FCSTD DOCUMENT  (FreeCAD 0.19R24291 (Git))
Label: Problem 10
License: All rights reserved
LicenseURL: http://en.wikipedia.org/wiki/All_rights_reserved
objects: Part::Part2DObjectPython×50, App::FeaturePython×45
note: 50 computed .brp shape members not serialized (recipe doc carries the construction recipe); baked Part::Feature solids carry a one-line shape summary decoded from their .brp

FEATURE [Part::Part2DObjectPython] Line  # Draft 2D object (typed FeaturePython)
  Area = 0
  ChamferSize = 0
  Closed = false
  End = (-61.5574,-5.46448,0)
  FilletRadius = 0
  Length = 23.4862
  MakeFace = false
  Placement = pos=(-143.431,-5.46448,0) rot=(0,0,1;0rad)
  Points = (2) [(58.3871,-3.55271e-15,0),(81.8734,-4.44089e-15,0)]
  Start = (-85.0436,-5.46448,0)
  Subdivisions = 0
FEATURE [Part::Part2DObjectPython] Wire  # Draft 2D object (typed FeaturePython)
  Area = 0
  ChamferSize = 0
  Closed = false
  End = (122.991,-5.46448,0)
  FilletRadius = 0
  Length = 125.6
  MakeFace = false
  Placement = pos=(-2.6087,-5.46448,0) rot=(0,0,1;0rad)
  Points = (3) [(0,0,0),(0,0,0),(125.6,3.55271e-15,0)]
  Start = (-2.6087,-5.46448,0)
  Subdivisions = 7
FEATURE [Part::Part2DObjectPython] Line008  # Draft 2D object (typed FeaturePython)
  Area = 0
  ChamferSize = 0
  Closed = false
  End = (-2.6087,13.1231,0)
  FilletRadius = 0
  Length = 18.5876
  MakeFace = false
  Placement = pos=(-2.6087,-5.46448,0) rot=(0,0,1;0rad)
  Points = (2) [(0,0,0),(4.44089e-16,18.5876,0)]
  Start = (-2.6087,-5.46448,0)
  Subdivisions = 0
FEATURE [Part::Part2DObjectPython] Line009  # Draft 2D object (typed FeaturePython)
  Area = 0
  ChamferSize = 0
  Closed = false
  End = (122.991,44.5355,0)
  FilletRadius = 0
  Length = 125.6
  MakeFace = false
  Points = (2) [(-2.6087,44.5355,0),(122.991,44.5355,0)]
  Start = (-2.6087,44.5355,0)
  Subdivisions = 0
FEATURE [Part::Part2DObjectPython] Line010  # Draft 2D object (typed FeaturePython)
  Area = 0
  ChamferSize = 0
  Closed = false
  End = (122.991,13.1231,0)
  FilletRadius = 0
  Length = 18.5876
  MakeFace = false
  Points = (2) [(122.991,-5.46448,0),(122.991,13.1231,0)]
  Start = (122.991,-5.46448,0)
  Subdivisions = 0
FEATURE [Part::Part2DObjectPython] Line011  # Draft 2D object (typed FeaturePython)
  Area = 0
  ChamferSize = 0
  Closed = false
  End = (60.1913,44.5355,0)
  FilletRadius = 0
  Length = 50
  MakeFace = false
  Placement = pos=(60.1913,-5.46448,0) rot=(0,0,1;0rad)
  Points = (2) [(0,0,0),(0,50,0)]
  Start = (60.1913,-5.46448,0)
  Subdivisions = 0
FEATURE [Part::Part2DObjectPython] Line012  # Draft 2D object (typed FeaturePython)
  Area = 0
  ChamferSize = 0
  Closed = false
  End = (13.0913,44.5355,0)
  FilletRadius = 0
  Length = 50
  MakeFace = false
  Placement = pos=(13.0913,-5.46448,0) rot=(0,0,1;0rad)
  Points = (2) [(0,0,0),(1.77636e-15,50,0)]
  Start = (13.0913,-5.46448,0)
  Subdivisions = 0
FEATURE [Part::Part2DObjectPython] Line013  # Draft 2D object (typed FeaturePython)
  Area = 0
  ChamferSize = 0
  Closed = false
  End = (28.7913,44.5355,0)
  FilletRadius = 0
  Length = 50
  MakeFace = false
  Placement = pos=(28.7913,-5.46448,0) rot=(0,0,1;0rad)
  Points = (2) [(0,0,0),(3.55271e-15,50,0)]
  Start = (28.7913,-5.46448,0)
  Subdivisions = 0
FEATURE [Part::Part2DObjectPython] Line014  # Draft 2D object (typed FeaturePython)
  Area = 0
  ChamferSize = 0
  Closed = false
  End = (44.4913,44.5355,0)
  FilletRadius = 0
  Length = 50
  MakeFace = false
  Placement = pos=(44.4913,-5.46448,0) rot=(0,0,1;0rad)
  Points = (2) [(0,0,0),(0,50,0)]
  Start = (44.4913,-5.46448,0)
  Subdivisions = 0
FEATURE [Part::Part2DObjectPython] Line015  # Draft 2D object (typed FeaturePython)
  Area = 0
  ChamferSize = 0
  Closed = false
  End = (75.8913,44.5355,0)
  FilletRadius = 0
  Length = 50
  MakeFace = false
  Placement = pos=(75.8913,-5.46448,0) rot=(0,0,1;0rad)
  Points = (2) [(0,0,0),(1.42109e-14,50,0)]
  Start = (75.8913,-5.46448,0)
  Subdivisions = 0
FEATURE [Part::Part2DObjectPython] Line016  # Draft 2D object (typed FeaturePython)
  Area = 0
  ChamferSize = 0
  Closed = false
  End = (91.5913,44.5355,0)
  FilletRadius = 0
  Length = 50
  MakeFace = false
  Placement = pos=(91.5913,-5.46448,0) rot=(0,0,1;0rad)
  Points = (2) [(0,0,0),(0,50,0)]
  Start = (91.5913,-5.46448,0)
  Subdivisions = 0
FEATURE [Part::Part2DObjectPython] Line017  # Draft 2D object (typed FeaturePython)
  Area = 0
  ChamferSize = 0
  Closed = false
  End = (107.291,44.5355,0)
  FilletRadius = 0
  Length = 50
  MakeFace = false
  Placement = pos=(107.291,-5.46448,0) rot=(0,0,1;0rad)
  Points = (2) [(0,0,0),(0,50,0)]
  Start = (107.291,-5.46448,0)
  Subdivisions = 0
FEATURE [Part::Part2DObjectPython] Circle  # Draft 2D object (typed FeaturePython)
  Area = 0
  FirstAngle = 0
  LastAngle = 0
  MakeFace = false
  Placement = pos=(-41.5574,-31.4208,0) rot=(0,0,1;0rad)
  Radius = 20
FEATURE [Part::Part2DObjectPython] Line018  # Draft 2D object (typed FeaturePython)
  Area = 0
  ChamferSize = 0
  Closed = false
  End = (-61.5574,-31.4208,0)
  FilletRadius = 0
  Length = 0
  MakeFace = false
  Placement = pos=(-61.5574,-31.4208,0) rot=(0,0,1;0rad)
  Points = (2) [(0,0,0),(0,-3.55271e-15,0)]
  Start = (-61.5574,-31.4208,0)
  Subdivisions = 0
FEATURE [Part::Part2DObjectPython] Line019  # Draft 2D object (typed FeaturePython)
  Area = 0
  ChamferSize = 0
  Closed = false
  End = (-61.6814,13.0515,0)
  FilletRadius = 0
  Length = 18.5161
  MakeFace = false
  Placement = pos=(-61.5574,-31.4208,0) rot=(0,0,1;0rad)
  Points = (2) [(-0.196875,25.9563,0),(-0.123968,44.4723,0)]
  Start = (-61.7543,-5.46448,0)
  Subdivisions = 0
FEATURE [Part::Part2DObjectPython] Line020  # Draft 2D object (typed FeaturePython)
  Area = 0
  ChamferSize = 0
  Closed = false
  End = (-41.5574,-5.46448,0)
  FilletRadius = 0
  Length = 50
  MakeFace = false
  Placement = pos=(-41.5574,-51.4208,0) rot=(0,0,1;0rad)
  Points = (2) [(-7.10543e-15,95.9563,0),(0,45.9563,0)]
  Start = (-41.5574,44.5355,0)
  Subdivisions = 0
FEATURE [Part::Part2DObjectPython] Line021  # Draft 2D object (typed FeaturePython)
  Area = 0
  ChamferSize = 0
  Closed = false
  End = (-55.6995,-5.46448,0)
  FilletRadius = 0
  Length = 50
  MakeFace = false
  Placement = pos=(-55.6995,-45.5629,0) rot=(0,0,1;0rad)
  Points = (2) [(0,90.0984,0),(0,40.0984,0)]
  Start = (-55.6995,44.5355,0)
  Subdivisions = 0
FEATURE [Part::Part2DObjectPython] Line022  # Draft 2D object (typed FeaturePython)
  Area = 0
  ChamferSize = 0
  Closed = false
  End = (-27.4152,-5.46448,0)
  FilletRadius = 0
  Length = 50
  MakeFace = false
  Placement = pos=(-27.4152,-45.5629,0) rot=(0,0,1;0rad)
  Points = (2) [(-1.42109e-14,90.0984,0),(0,40.0984,0)]
  Start = (-27.4152,44.5355,0)
  Subdivisions = 0
FEATURE [Part::Part2DObjectPython] Line023  # Draft 2D object (typed FeaturePython)
  Area = 0
  ChamferSize = 0
  Closed = false
  End = (-21.5574,36.2171,0)
  FilletRadius = 0
  Length = 8.31841
  MakeFace = false
  Placement = pos=(-21.5574,-31.4208,0) rot=(0,0,1;0rad)
  Points = (2) [(-4.26326e-14,75.9563,0),(-2.4869e-14,67.6379,0)]
  Start = (-21.5574,44.5355,0)
  Subdivisions = 0
FEATURE [Part::Part2DObjectPython] Line024  # Draft 2D object (typed FeaturePython)
  Area = 0
  ChamferSize = 0
  Closed = false
  End = (-61.5574,44.5355,0)
  FilletRadius = 0
  Length = 40
  MakeFace = false
  Placement = pos=(-21.5574,44.5355,0) rot=(0,0,1;0rad)
  Points = (2) [(0,0,0),(-40,-7.10543e-15,0)]
  Start = (-21.5574,44.5355,0)
  Subdivisions = 0
FEATURE [Part::Part2DObjectPython] Line026  # Draft 2D object (typed FeaturePython)
  Area = 0
  ChamferSize = 0
  Closed = false
  End = (-21.5574,36.2171,0)
  FilletRadius = 0
  Length = 11.8769
  MakeFace = false
  Placement = pos=(-41.5886,24.6521,0) rot=(0,0,1;0.523599rad)
  Points = (2) [(35.007,2.13163e-14,0),(23.1301,2.84217e-14,0)]
  Start = (-11.2717,42.1556,0)
  Subdivisions = 0
FEATURE [Part::Part2DObjectPython] Line027  # Draft 2D object (typed FeaturePython)
  Area = 0
  ChamferSize = 0
  Closed = false
  End = (122.991,13.1231,0)
  FilletRadius = 0
  Length = 184.549
  MakeFace = false
  Placement = pos=(-61.5574,13.1231,0) rot=(0,0,1;0rad)
  Points = (2) [(0,0,0),(184.549,-5.32907e-15,0)]
  Start = (-61.5574,13.1231,0)
  Subdivisions = 0
FEATURE [Part::Part2DObjectPython] Line028  # Draft 2D object (typed FeaturePython)
  Area = 0
  ChamferSize = 0
  Closed = false
  End = (122.991,16.5051,0)
  FilletRadius = 0
  Length = 178.691
  MakeFace = false
  Placement = pos=(-55.6995,16.5051,0) rot=(0,0,1;0rad)
  Points = (2) [(0,0,0),(178.691,1.06581e-14,0)]
  Start = (-55.6995,16.5051,0)
  Subdivisions = 0
FEATURE [Part::Part2DObjectPython] Line029  # Draft 2D object (typed FeaturePython)
  Area = 0
  ChamferSize = 0
  Closed = false
  End = (122.991,24.6701,0)
  FilletRadius = 0
  Length = 164.549
  MakeFace = false
  Placement = pos=(-41.5574,24.6701,0) rot=(0,0,1;0rad)
  Points = (2) [(0,0,0),(164.549,-7.10543e-15,0)]
  Start = (-41.5574,24.6701,0)
  Subdivisions = 0
FEATURE [Part::Part2DObjectPython] Line030  # Draft 2D object (typed FeaturePython)
  Area = 0
  ChamferSize = 0
  Closed = false
  End = (122.991,32.8351,0)
  FilletRadius = 0
  Length = 150.407
  MakeFace = false
  Placement = pos=(-27.4152,32.8351,0) rot=(0,0,1;0rad)
  Points = (2) [(0,0,0),(150.407,-7.10543e-15,0)]
  Start = (-27.4152,32.8351,0)
  Subdivisions = 0
FEATURE [Part::Part2DObjectPython] Line031  # Draft 2D object (typed FeaturePython)
  Area = 0
  ChamferSize = 0
  Closed = false
  End = (122.991,36.2171,0)
  FilletRadius = 0
  Length = 144.549
  MakeFace = false
  Placement = pos=(-21.5574,36.2171,0) rot=(0,0,1;0rad)
  Points = (2) [(0,0,0),(144.549,7.10543e-15,0)]
  Start = (-21.5574,36.2171,0)
  Subdivisions = 0
FEATURE [Part::Part2DObjectPython] Line032  # Draft 2D object (typed FeaturePython)
  Area = 0
  ChamferSize = 0
  Closed = false
  End = (-2.6087,44.5355,0)
  FilletRadius = 0
  Length = 31.4124
  MakeFace = false
  Placement = pos=(-2.6087,-5.46448,0) rot=(0,0,1;0rad)
  Points = (2) [(4.44089e-16,18.5876,0),(1.33227e-15,50,0)]
  Start = (-2.6087,13.1231,0)
  Subdivisions = 0
FEATURE [Part::Part2DObjectPython] Line033  # Draft 2D object (typed FeaturePython)
  Area = 0
  ChamferSize = 0
  Closed = false
  End = (122.991,44.5355,0)
  FilletRadius = 0
  Length = 31.4124
  MakeFace = false
  Points = (2) [(122.991,13.1231,0),(122.991,44.5355,0)]
  Start = (122.991,13.1231,0)
  Subdivisions = 0
FEATURE [Part::Part2DObjectPython] Line034  # Draft 2D object (typed FeaturePython)
  Area = 0
  ChamferSize = 0
  Closed = false
  End = (-61.6814,13.0515,0)
  FilletRadius = 0
  Length = 0.143146
  MakeFace = false
  Placement = pos=(-41.5886,24.6521,0) rot=(0,0,1;0.523599rad)
  Points = (2) [(-23.0579,2.13163e-14,0),(-23.2011,2.84217e-14,0)]
  Start = (-61.5574,13.1231,0)
  Subdivisions = 0
FEATURE [Part::Part2DObjectPython] Line035  # Draft 2D object (typed FeaturePython)
  Area = 0
  ChamferSize = 0
  Closed = false
  End = (-61.5574,13.1231,0)
  FilletRadius = 0
  Length = 46.188
  MakeFace = false
  Placement = pos=(-41.5886,24.6521,0) rot=(0,0,1;0.523599rad)
  Points = (2) [(23.1301,3.55271e-14,0),(-23.0579,2.13163e-14,0)]
  Start = (-21.5574,36.2171,0)
  Subdivisions = 0
FEATURE [Part::Part2DObjectPython] Line036  # Draft 2D object (typed FeaturePython)
  Area = 0
  ChamferSize = 0
  Closed = false
  End = (-61.5574,-31.4208,0)
  FilletRadius = 0
  Length = 25.9563
  MakeFace = false
  Placement = pos=(-61.5574,-31.4208,0) rot=(0,0,1;0rad)
  Points = (2) [(7.10543e-15,25.9563,0),(0,7.10543e-15,0)]
  Start = (-61.5574,-5.46448,0)
  Subdivisions = 0
FEATURE [Part::Part2DObjectPython] Line037  # Draft 2D object (typed FeaturePython)
  Area = 0
  ChamferSize = 0
  Closed = false
  End = (-21.5574,-31.4208,0)
  FilletRadius = 0
  Length = 25.9563
  MakeFace = false
  Placement = pos=(-21.5574,-31.4208,0) rot=(0,0,1;0rad)
  Points = (2) [(-1.42109e-14,25.9563,0),(0,-3.55271e-15,0)]
  Start = (-21.5574,-5.46448,0)
  Subdivisions = 0
FEATURE [Part::Part2DObjectPython] Line038  # Draft 2D object (typed FeaturePython)
  Area = 0
  ChamferSize = 0
  Closed = false
  End = (-21.5574,-5.46448,0)
  FilletRadius = 0
  Length = 40
  MakeFace = false
  Placement = pos=(-143.431,-5.46448,0) rot=(0,0,1;0rad)
  Points = (2) [(81.8734,-4.44089e-15,0),(121.873,5.32907e-15,0)]
  Start = (-61.5574,-5.46448,0)
  Subdivisions = 0
FEATURE [Part::Part2DObjectPython] Line039  # Draft 2D object (typed FeaturePython)
  Area = 0
  ChamferSize = 0
  Closed = false
  End = (-21.5574,-5.46448,0)
  FilletRadius = 0
  Length = 14.9371
  MakeFace = false
  Placement = pos=(-143.431,-5.46448,0) rot=(0,0,1;0rad)
  Points = (2) [(136.811,4.44089e-15,0),(121.873,5.32907e-15,0)]
  Start = (-6.62024,-5.46448,0)
  Subdivisions = 0
FEATURE [App::FeaturePython] Text  # WARN: FeaturePython — macro-defined, semantics opaque (R4)
  Placement = pos=(-3.28307,-10.6789,0) rot=(0,0,1;0rad)
  Text = A
FEATURE [App::FeaturePython] Text001  # WARN: FeaturePython — macro-defined, semantics opaque (R4)
  Placement = pos=(12.4016,-9.67778,0) rot=(0,0,1;0rad)
  Text = B
FEATURE [App::FeaturePython] Text002  # WARN: FeaturePython — macro-defined, semantics opaque (R4)
  Placement = pos=(28.0863,-10.0115,0) rot=(0,0,1;0rad)
  Text = C
FEATURE [App::FeaturePython] Text003  # WARN: FeaturePython — macro-defined, semantics opaque (R4)
  Placement = pos=(43.4373,-10.0115,0) rot=(0,0,1;0rad)
  Text = D
FEATURE [App::FeaturePython] Text004  # WARN: FeaturePython — macro-defined, semantics opaque (R4)
  Placement = pos=(59.2888,-10.6789,0) rot=(0,0,1;0rad)
  Text = E
FEATURE [App::FeaturePython] Text005  # WARN: FeaturePython — macro-defined, semantics opaque (R4)
  Placement = pos=(75.3072,-10.0115,0) rot=(0,0,1;0rad)
  Text = F
FEATURE [App::FeaturePython] Text006  # WARN: FeaturePython — macro-defined, semantics opaque (R4)
  Placement = pos=(90.825,-10.5121,0) rot=(0,0,1;0rad)
  Text = G
FEATURE [App::FeaturePython] Text007  # WARN: FeaturePython — macro-defined, semantics opaque (R4)
  Placement = pos=(106.009,-10.1784,0) rot=(0,0,1;0rad)
  Text = H
FEATURE [App::FeaturePython] Text008  # WARN: FeaturePython — macro-defined, semantics opaque (R4)
  Placement = pos=(121.861,-10.0115,0) rot=(0,0,1;0rad)
  Text = A
FEATURE [App::FeaturePython] Text009  # WARN: FeaturePython — macro-defined, semantics opaque (R4)
  Placement = pos=(-64.5201,-30.2014,0) rot=(0,0,1;0rad)
  Text = a
FEATURE [App::FeaturePython] Text010  # WARN: FeaturePython — macro-defined, semantics opaque (R4)
  Placement = pos=(-57.512,-48.0552,0) rot=(0,0,1;0rad)
  Text = b
FEATURE [App::FeaturePython] Text011  # WARN: FeaturePython — macro-defined, semantics opaque (R4)
  Placement = pos=(-41.9942,-55.8975,0) rot=(0,0,1;0rad)
  Text = c
FEATURE [App::FeaturePython] Text012  # WARN: FeaturePython — macro-defined, semantics opaque (R4)
  Placement = pos=(-26.4764,-49.0563,0) rot=(0,0,1;0rad)
  Text = d
FEATURE [App::FeaturePython] Text013  # WARN: FeaturePython — macro-defined, semantics opaque (R4)
  Placement = pos=(-20.8032,-31.7031,0) rot=(0,0,1;0rad)
  Text = e
FEATURE [App::FeaturePython] Text014  # WARN: FeaturePython — macro-defined, semantics opaque (R4)
  Placement = pos=(-26.8101,-17.1864,0) rot=(0,0,1;0rad)
  Text = f
FEATURE [App::FeaturePython] Text015  # WARN: FeaturePython — macro-defined, semantics opaque (R4)
  Placement = pos=(-40.6593,-10.5121,0) rot=(0,0,1;0rad)
  Text = g
FEATURE [App::FeaturePython] Text016  # WARN: FeaturePython — macro-defined, semantics opaque (R4)
  Placement = pos=(-58.3463,-17.5201,0) rot=(0,0,1;0rad)
  Text = h
FEATURE [App::FeaturePython] Text017  # WARN: FeaturePython — macro-defined, semantics opaque (R4)
  Placement = pos=(-4.95165,13.3487,0) rot=(0,0,1;0rad)
  Text = 1
FEATURE [App::FeaturePython] Text018  # WARN: FeaturePython — macro-defined, semantics opaque (R4)
  Placement = pos=(10.733,17.0195,0) rot=(0,0,1;0rad)
  Text = 2
FEATURE [App::FeaturePython] Text019  # WARN: FeaturePython — macro-defined, semantics opaque (R4)
  Placement = pos=(26.5846,25.1956,0) rot=(0,0,1;0rad)
  Text = 3
FEATURE [App::FeaturePython] Text020  # WARN: FeaturePython — macro-defined, semantics opaque (R4)
  Placement = pos=(41.7687,33.3717,0) rot=(0,0,1;0rad)
  Text = 4
FEATURE [App::FeaturePython] Text021  # WARN: FeaturePython — macro-defined, semantics opaque (R4)
  Placement = pos=(57.6202,36.7088,0) rot=(0,0,1;0rad)
  Text = 5
FEATURE [App::FeaturePython] Text022  # WARN: FeaturePython — macro-defined, semantics opaque (R4)
  Placement = pos=(76.8089,33.5385,0) rot=(0,0,1;0rad)
  Text = 6
FEATURE [App::FeaturePython] Text023  # WARN: FeaturePython — macro-defined, semantics opaque (R4)
  Placement = pos=(92.4936,25.3625,0) rot=(0,0,1;0rad)
  Text = 7
FEATURE [App::FeaturePython] Text024  # WARN: FeaturePython — macro-defined, semantics opaque (R4)
  Placement = pos=(107.845,17.3533,0) rot=(0,0,1;0rad)
  Text = 8
FEATURE [App::FeaturePython] Text025  # WARN: FeaturePython — macro-defined, semantics opaque (R4)
  Placement = pos=(-66.1886,12.1807,0) rot=(0,0,1;0rad)
  Text = 1'
FEATURE [App::FeaturePython] Text026  # WARN: FeaturePython — macro-defined, semantics opaque (R4)
  Placement = pos=(-59.6812,16.519,0) rot=(0,0,1;0rad)
  Text = 2'
FEATURE [App::FeaturePython] Text027  # WARN: FeaturePython — macro-defined, semantics opaque (R4)
  Placement = pos=(-46.1656,24.5282,0) rot=(0,0,1;0rad)
  Text = 3'
FEATURE [App::FeaturePython] Text028  # WARN: FeaturePython — macro-defined, semantics opaque (R4)
  Placement = pos=(-31.8158,32.2037,0) rot=(0,0,1;0rad)
  Text = 4'
FEATURE [App::FeaturePython] Text029  # WARN: FeaturePython — macro-defined, semantics opaque (R4)
  Placement = pos=(-20.3026,38.3774,0) rot=(0,0,1;0rad)
  Text = 5'
FEATURE [App::FeaturePython] Text030  # WARN: FeaturePython — macro-defined, semantics opaque (R4)
  Placement = pos=(-65.688,-5.17261,0) rot=(0,0,1;0rad)
  Text = a'
FEATURE [App::FeaturePython] Text031  # WARN: FeaturePython — macro-defined, semantics opaque (R4)
  Placement = pos=(-59.5143,-5.17261,0) rot=(0,0,1;0rad)
  Text = b'(h')
FEATURE [App::FeaturePython] Text032  # WARN: FeaturePython — macro-defined, semantics opaque (R4)
  Placement = pos=(-44.9976,-4.00459,0) rot=(0,0,1;0rad)
  Text = c'(g')
FEATURE [App::FeaturePython] Text033  # WARN: FeaturePython — macro-defined, semantics opaque (R4)
  Placement = pos=(-31.4821,-4.83889,0) rot=(0,0,1;0rad)
  Text = d'(f')
FEATURE [App::FeaturePython] Text034  # WARN: FeaturePython — macro-defined, semantics opaque (R4)
  Placement = pos=(-19.9689,-5.17261,0) rot=(0,0,1;0rad)
  Text = e'
FEATURE [App::FeaturePython] Text035  # WARN: FeaturePython — macro-defined, semantics opaque (R4)
  Placement = pos=(-26.6432,28.6996,0) rot=(0,0,1;0rad)
  Text = (6')
FEATURE [App::FeaturePython] Text036  # WARN: FeaturePython — macro-defined, semantics opaque (R4)
  Placement = pos=(-40.6593,21.191,0) rot=(0,0,1;0rad)
  Text = (7')
FEATURE [App::FeaturePython] Text037  # WARN: FeaturePython — macro-defined, semantics opaque (R4)
  Placement = pos=(-54.1748,13.3487,0) rot=(0,0,1;0rad)
  Text = (8')
FEATURE [App::FeaturePython] Text038  # WARN: FeaturePython — macro-defined, semantics opaque (R4)
  Placement = pos=(25.2497,-38.5443,0) rot=(0,0,1;0rad)
  Text = ALL DIMENSIONS ARE IN mm
FEATURE [Part::Part2DObjectPython] Line041  # Draft 2D object (typed FeaturePython)
  Area = 0
  ChamferSize = 0
  Closed = false
  End = (-21.5574,-5.46448,0)
  FilletRadius = 0
  Length = 41.6816
  MakeFace = false
  Placement = pos=(-21.5574,-31.4208,0) rot=(0,0,1;0rad)
  Points = (2) [(-2.84217e-14,67.6379,0),(-1.42109e-14,25.9563,0)]
  Start = (-21.5574,36.2171,0)
  Subdivisions = 0
FEATURE [Part::Part2DObjectPython] Line042  # Draft 2D object (typed FeaturePython)
  Area = 0
  ChamferSize = 0
  Closed = false
  End = (-61.6814,13.0515,0)
  FilletRadius = 0
  Length = 20.3939
  MakeFace = false
  Placement = pos=(-41.5886,24.6521,0) rot=(0,0,1;0.523599rad)
  Points = (2) [(-43.595,4.26326e-14,0),(-23.2011,2.84217e-14,0)]
  Start = (-79.343,2.85455,0)
  Subdivisions = 0
FEATURE [Part::Part2DObjectPython] Line043  # Draft 2D object (typed FeaturePython)
  Area = 0
  ChamferSize = 0
  Closed = false
  End = (-61.5574,44.5355,0)
  FilletRadius = 0
  Length = 31.4842
  MakeFace = false
  Placement = pos=(-61.5574,-31.4208,0) rot=(0,0,1;0rad)
  Points = (2) [(-0.123968,44.4723,0),(0,75.9563,0)]
  Start = (-61.6814,13.0515,0)
  Subdivisions = 0
FEATURE [Part::Part2DObjectPython] BSpline  # Draft 2D object (typed FeaturePython)
  Area = 0
  Closed = false
  MakeFace = false
  Parameterization = 1
  Points = (9) [(-2.6087,13.1231,0),(13.0913,16.5051,0),(28.7913,24.6701,0),(44.4913,32.8351,0),(60.1913,36.2171,0),(75.8913,32.8351,0),(91.5913,24.6701,0),(107.291,16.5051,0),(122.991,13.1231,0)]
FEATURE [App::FeaturePython] Dimension  # Draft dimension (typed FeaturePython)
  Diameter = false
  Dimline = (-9.1231,-4.17146,0)
  Direction = (0,0,0)
  Distance = 30.1346
  End = (-2.6087,-5.46448,0)
  Normal = (0,0,1)
  Start = (-2.6087,24.6701,0)
FEATURE [App::FeaturePython] Dimension001  # Draft dimension (typed FeaturePython)
  Diameter = false
  Dimline = (-78.5362,-0.500574,0)
  Direction = (0,0,0)
  Distance = 50.0004
  End = (-61.7543,-5.46448,0)
  Normal = (0,0,1)
  Start = (-61.5574,44.5355,0)
FEATURE [App::FeaturePython] Dimension002  # Draft dimension (typed FeaturePython)
  Diameter = false
  Dimline = (120.025,-24.1945,0)
  Direction = (0,0,0)
  Distance = 125.6
  End = (122.991,-5.46448,0)
  Normal = (0,0,1)
  Start = (-2.6087,-5.46448,0)
FEATURE [Part::Part2DObjectPython] Line044  # Draft 2D object (typed FeaturePython)
  Area = 0
  ChamferSize = 0
  Closed = false
  End = (-27.4152,-45.5629,0)
  FilletRadius = 0
  Length = 40
  MakeFace = false
  Placement = pos=(-55.6995,-17.2786,0) rot=(0,0,1;0rad)
  Points = (2) [(0,0,0),(28.2843,-28.2843,0)]
  Start = (-55.6995,-17.2786,0)
  Subdivisions = 0
FEATURE [Part::Part2DObjectPython] Line045  # Draft 2D object (typed FeaturePython)
  Area = 0
  ChamferSize = 0
  Closed = false
  End = (-27.4152,-17.2786,0)
  FilletRadius = 0
  Length = 40
  MakeFace = false
  Placement = pos=(-27.4152,-17.2786,0) rot=(0,0,1;0rad)
  Points = (2) [(0,0,0),(0,-3.55271e-15,0)]
  Start = (-27.4152,-17.2786,0)
  Subdivisions = 0
FEATURE [Part::Part2DObjectPython] Line046  # Draft 2D object (typed FeaturePython)
  Area = 0
  ChamferSize = 0
  Closed = false
  End = (-21.5574,-31.4208,0)
  FilletRadius = 0
  Length = 40
  MakeFace = false
  Placement = pos=(-61.5574,-31.4208,0) rot=(0,0,1;0rad)
  Points = (2) [(0,0,0),(40,-1.77636e-14,0)]
  Start = (-61.5574,-31.4208,0)
  Subdivisions = 0
FEATURE [Part::Part2DObjectPython] Line047  # Draft 2D object (typed FeaturePython)
  Area = 0
  ChamferSize = 0
  Closed = false
  End = (-55.6995,-17.2786,0)
  FilletRadius = 0
  Length = 11.8141
  MakeFace = false
  Placement = pos=(-55.6995,-45.5629,0) rot=(0,0,1;0rad)
  Points = (2) [(0,40.0984,0),(0,28.2843,0)]
  Start = (-55.6995,-5.46448,0)
  Subdivisions = 0
FEATURE [Part::Part2DObjectPython] Line048  # Draft 2D object (typed FeaturePython)
  Area = 0
  ChamferSize = 0
  Closed = false
  End = (-41.5574,-11.4208,0)
  FilletRadius = 0
  Length = 5.95628
  MakeFace = false
  Placement = pos=(-41.5574,-51.4208,0) rot=(0,0,1;0rad)
  Points = (2) [(0,45.9563,0),(0,40,0)]
  Start = (-41.5574,-5.46448,0)
  Subdivisions = 0
FEATURE [Part::Part2DObjectPython] Line049  # Draft 2D object (typed FeaturePython)
  Area = 0
  ChamferSize = 0
  Closed = false
  End = (-27.4152,-17.2786,0)
  FilletRadius = 0
  Length = 11.8141
  MakeFace = false
  Placement = pos=(-27.4152,-45.5629,0) rot=(0,0,1;0rad)
  Points = (2) [(0,40.0984,0),(0,28.2843,0)]
  Start = (-27.4152,-5.46448,0)
  Subdivisions = 0
FEATURE [Part::Part2DObjectPython] Line050  # Draft 2D object (typed FeaturePython)
  Area = 0
  ChamferSize = 0
  Closed = false
  End = (-55.6995,-45.5629,0)
  FilletRadius = 0
  Length = 40
  MakeFace = false
  Placement = pos=(-27.4152,-17.2786,0) rot=(0,0,1;0rad)
  Points = (2) [(0,-3.55271e-15,0),(-28.2843,-28.2843,0)]
  Start = (-27.4152,-17.2786,0)
  Subdivisions = 0
FEATURE [Part::Part2DObjectPython] Line051  # Draft 2D object (typed FeaturePython)
  Area = 0
  ChamferSize = 0
  Closed = false
  End = (-41.5574,-51.4208,0)
  FilletRadius = 0
  Length = 40
  MakeFace = false
  Placement = pos=(-41.5574,-51.4208,0) rot=(0,0,1;0rad)
  Points = (2) [(0,40,0),(0,-7.10543e-15,0)]
  Start = (-41.5574,-11.4208,0)
  Subdivisions = 0
FEATURE [Part::Part2DObjectPython] Line052  # Draft 2D object (typed FeaturePython)
  Area = 0
  ChamferSize = 0
  Closed = false
  End = (-55.6995,-45.5629,0)
  FilletRadius = 0
  Length = 28.2843
  MakeFace = false
  Placement = pos=(-55.6995,-45.5629,0) rot=(0,0,1;0rad)
  Points = (2) [(0,28.2843,0),(0,7.10543e-15,0)]
  Start = (-55.6995,-17.2786,0)
  Subdivisions = 0
FEATURE [Part::Part2DObjectPython] Line053  # Draft 2D object (typed FeaturePython)
  Area = 0
  ChamferSize = 0
  Closed = false
  End = (-27.4152,-45.5629,0)
  FilletRadius = 0
  Length = 28.2843
  MakeFace = false
  Placement = pos=(-27.4152,-45.5629,0) rot=(0,0,1;0rad)
  Points = (2) [(0,28.2843,0),(0,0,0)]
  Start = (-27.4152,-17.2786,0)
  Subdivisions = 0
FEATURE [App::FeaturePython] Dimension003  # Draft dimension (typed FeaturePython)
  Angle = 30
  Center = (-93.752,-5.46448,0)
  Dimline = (-71.695,-3.00345,0)
  FirstAngle = 360
  LastAngle = 30
  Normal = (0,0,1)
FEATURE [Part::Part2DObjectPython] Line054  # Draft 2D object (typed FeaturePython)
  Area = 0
  ChamferSize = 0
  Closed = false
  End = (-68.5803,9.06842,0)
  FilletRadius = 0
  Length = 9.56651
  MakeFace = false
  Placement = pos=(-73.3635,17.3533,0) rot=(0,0,1;0rad)
  Points = (2) [(0,0,0),(4.78326,-8.28484,0)]
  Start = (-73.3635,17.3533,0)
  Subdivisions = 0
FEATURE [Part::Part2DObjectPython] Line055  # Draft 2D object (typed FeaturePython)
  Area = 0
  ChamferSize = 0
  Closed = false
  End = (-13.2145,41.0339,0)
  FilletRadius = 0
  Length = 9.56651
  MakeFace = false
  Points = (2) [(-17.9978,49.3187,0),(-13.2145,41.0339,0)]
  Start = (-17.9978,49.3187,0)
  Subdivisions = 0
FEATURE [App::FeaturePython] Text039  # WARN: FeaturePython — macro-defined, semantics opaque (R4)
  Placement = pos=(-75.199,17.687,0) rot=(0,0,1;0rad)
  Text = S
FEATURE [App::FeaturePython] Text040  # WARN: FeaturePython — macro-defined, semantics opaque (R4)
  Placement = pos=(-18.4672,50.2243,0) rot=(0,0,1;0rad)
  Text = P
